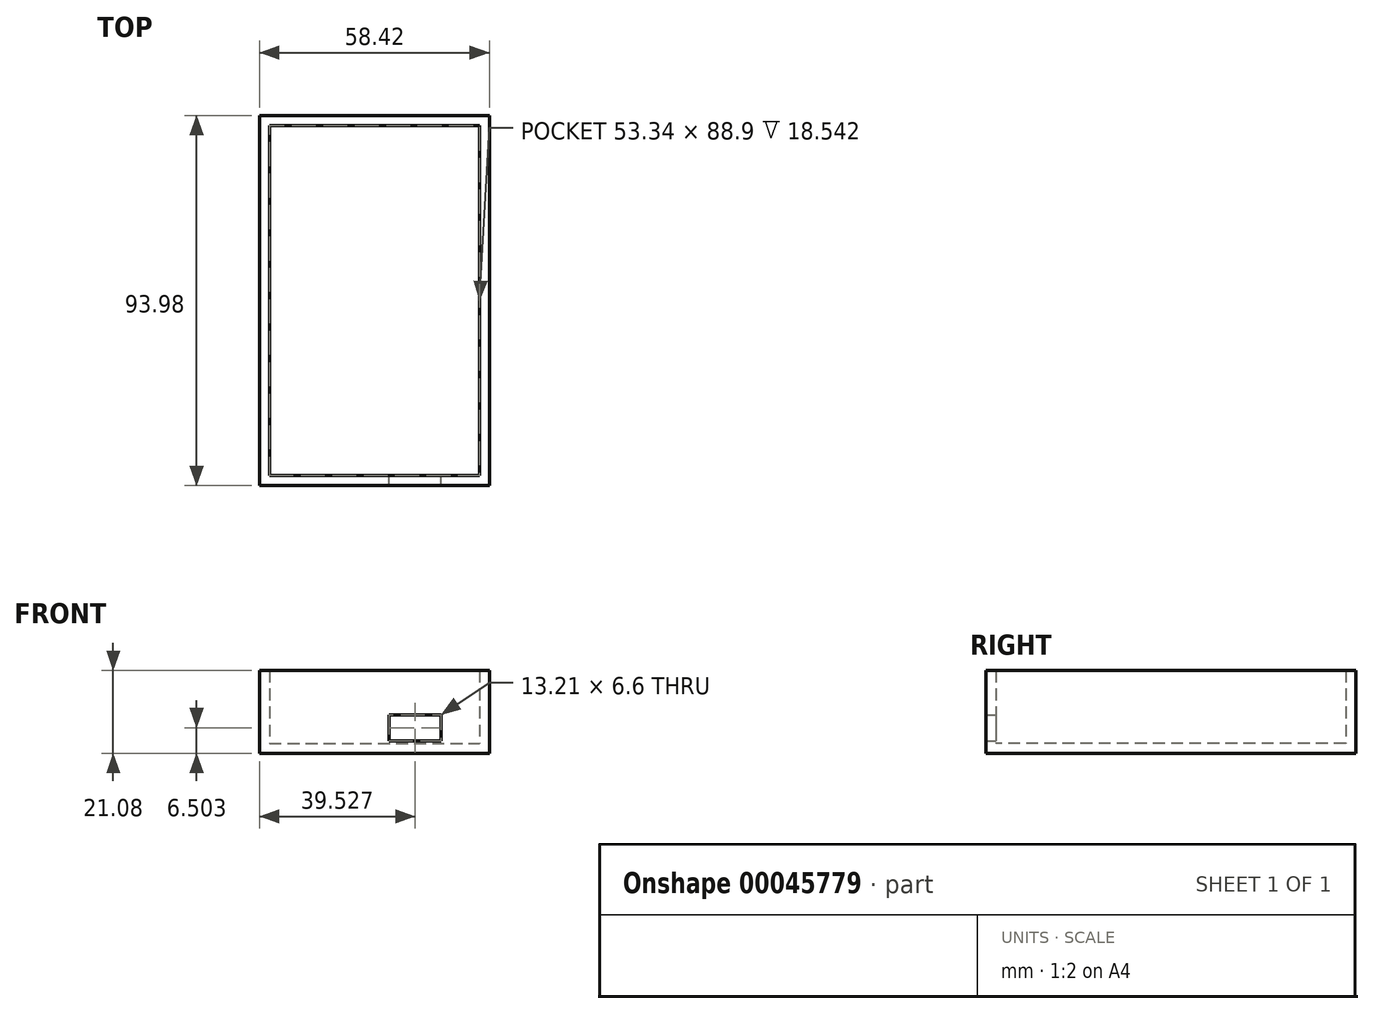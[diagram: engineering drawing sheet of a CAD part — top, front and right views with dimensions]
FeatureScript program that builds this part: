
annotation { "Feature Type Name" : "Feature", "Feature Type Description" : "" }
export const myFeature = defineFeature(function(context is Context, id is Id, definition is map)
    precondition{}
    {
        {
            var Q0;
            Q0=qCreatedBy(makeId("Top.planeOp"),FACE);
            var sketch = newSketch(context, id + "F0", { "sketchPlane" : qUnion([Q0])});
            skLineSegment(sketch, "E0.bottom", {"start": v(-20.84, 80.37) * mm, "end": v(37.58, 80.37) * mm});
            skLineSegment(sketch, "E0.top", {"start": v(-20.84, -13.6) * mm, "end": v(37.58, -13.6) * mm});
            skLineSegment(sketch, "E0.left", {"start": v(-20.84, 80.37) * mm, "end": v(-20.84, -13.6) * mm});
            skLineSegment(sketch, "E0.right", {"start": v(37.58, 80.37) * mm, "end": v(37.58, -13.6) * mm});
            skSolve(sketch);
        }
        {
            var Q0;
            Q0=makeQuery(id+"F0.imprint","IMPRINT",FACE,{"disambiguationData":[TD([[makeQuery(id+"F0.imprint","IMPRINT",EDGE,{"derivedFrom":sQuery(id+"F0.wireOp",EDGE,"E0.bottom")}),-1.0]])]});
            extrude(context, id + "F1", {"entities" : qUnion([Q0]), "depth" : 21.08 * mm});
        }
        {
            var Q0;
            Q0=makeQuery(id+"F1.opExtrude","CAP_FACE",FACE,{"disambiguationData":[OSD([sQuery(id+"F0.wireOp",EDGE,"E0.bottom"),sQuery(id+"F0.wireOp",EDGE,"E0.top"),sQuery(id+"F0.wireOp",EDGE,"E0.left"),sQuery(id+"F0.wireOp",EDGE,"E0.right")])],"isStart":false});
            shell(context, id + "F2", {"entities" : qUnion([Q0]), "thickness" : 2.54 * mm});
        }
        {
            var Q0;
            Q0=qCreatedBy(makeId("Front.planeOp"),FACE);
            var sketch = newSketch(context, id + "F3", { "sketchPlane" : qUnion([Q0])});
            skLineSegment(sketch, "E1.bottom", {"start": v(12.08, 9.8) * mm, "end": v(25.3, 9.8) * mm});
            skLineSegment(sketch, "E1.top", {"start": v(12.08, 3.2) * mm, "end": v(25.3, 3.2) * mm});
            skLineSegment(sketch, "E1.left", {"start": v(12.08, 9.8) * mm, "end": v(12.08, 3.2) * mm});
            skLineSegment(sketch, "E1.right", {"start": v(25.3, 9.8) * mm, "end": v(25.3, 3.2) * mm});
            skSolve(sketch);
        }
        {
            var Q0;
            Q0 = qSketchRegion(id + "F3", true);
            extrude(context, id + "F4", {"entities" : qUnion([Q0]), "operationType" : NewBodyOperationType.REMOVE, "depth" : 44.38 * mm});
        }
    });
